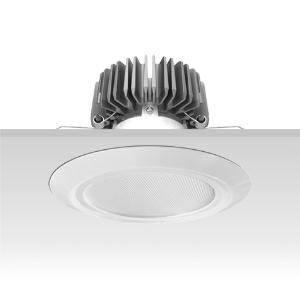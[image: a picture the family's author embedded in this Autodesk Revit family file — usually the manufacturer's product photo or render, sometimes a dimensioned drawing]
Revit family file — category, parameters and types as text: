
# Revit family: 3f_filippi_-_3f_reno_bianco_ampio_3f_filippi_-_30633_a01048_-_3f_reno_200_wh_3000-930_wide___smp_wh_855b
name_source: partatom
category: Lighting Fixtures
units: mm (PartAtom-declared; Revit-internal decimal feet)

## family parameters
Cut with Voids When Loaded = No
Host = Face
Light Source = No
Part Type = Normal
Room Calculation Point = No
Round Connector Dimension = Use Diameter
Shared = No

## types (1)
- 3F Filippi - 3F Reno Bianco Ampio (1 x LED, 2320 lm, 37 W, 3000 K)
    Apparent Load = 37 VA
    Approval mark = CE
    CIE Flux Codes = 74 92 98 100 100
    Color Rendering = 90
    Color Temperature = 3000 K
    Control Gear = Electronic ballast
    Default Elevation = 1800 mm
    Description = ILLUMINOTECHNICAL
Luminous efficiency 100% (DLOR 100%, ULOR 0%).
Initial luminous flux of the luminaire 2320 lm.
Direct symmetric wide distribution.
Installation Interdistance Transv.D = 1.06 x hu - Long.D = 1.04 x hu.
Tabular UGR (CIE 117 - 4H-8H; S=0.25H; 70/50/20): RUG 22.5 - 22.3.
Beam angle: 70° - 69°.
Luminous efficacy 63 lm/W.
Lifetime (L90/B10): 30000 h. (tq+25°C)
Lifetime (L85/B10): 50000 h. (tq+25°C)
Lifetime (L70/B10): 80000 h. (tq+25°C)
Sudden decreased luminous flux after 50000 hours: 0% (C0).
Photobiological safety in compliance with IEC/TR 62778: RG0 risk exempt, (IEC 62471).
In compliance with IEC/EN 62722-2-1 - IEC/EN 62717 standards.

SOURCE
Compact LED module 3000/930.
Energy efficiency class (UE 2019/2020 - UE 2019/2015): E.
CIE 13.3 Colour rendering index: CRI >90 (R9 >50%).
IES TM-30 Fidelity Index: Rf = 92 Rg = 101.
CCT nominal colour temperature 3000 K.
Colour initial tolerance (MacAdam): SDCM 3.
Zhaga Book 3 compliant.

MECHANICAL
Passive heat dissipator in die-casting aluminium, oversized, for optimum thermal management of the LED module.
Parabolic element with graduated/concentric rings in white polycarbonate.
Transparent external lens with glossy and satin differentiated surfaces, with a cooling and anti-insect system in methacrylate (PMMA).
Fastening spring clips in stainless steel.
Dimensions: diameter 226 mm, height 146 mm. Weight 1.645 kg.
IP44 protection degree for exposed part, IP20 for recessed part.
Mechanical strength to impacts IK05 (0.7 joule).
Glow-wire test resistance 650°C.

ELECTRICAL
Wiring on a separate unit.
Halogen Free electronic wiring 230V-50/60Hz, power factor 0.95, THD <25%, constant output current, SELV, class II, 1 driver.
Power of the luminaire 37 W.
ENEC - CE.
SAFE FLICKER: PstLM=<1 and SVM=<0.4 (IEC TR 61547-1 and IEC TR 63158), to ensure a more comfortable and safe light.
Luminaire compliant with EN 60598-2-22 for power supply from a centralised emergency system CPSS (Central Power Supply System), not incorporated in the luminaire - high risk areas excluded. The default power and flux are 100% in AC and 100% in DC.
Ambient temperature from 0°C to +25°C.
Temperature class T6 max 85°C.
Relative humidity UR: <85%.

INSTALLATION
Pull-up recessed fitting.
False ceiling carving: 200 mm.
All accessories dedicated to this product are available on the Catalog and on our website www.3F-Filippi.com.

ACCESSORIES
A01048 - Anti-glare microprismatic SMP diffuser in methacrylate (PMMA), locked and in line with the trim, in white polycarbonate.

APPLICATIONS
Suitable product for food production plants (HACCP), IFS (Food Version 6), BRC (GSFS Food Version 7).
Environments: architectural, commercial, exhibition areas, transit areas, corridors, shops, display windows, service areas.
In false ceilings with narrow voids.

WARNING
Luminaire designed for disposal/recycling at end-of-life.
Replaceable (LED only) light source by a professional. Replaceable control gear by a professional.
    Height = 0 mm  [stored 0 ft]
    Lamp = 1 x LED
    Lamp Light Flux = 2320 lm
    Lamp Power = 37 W
    Lamp count = 1
    Length = 226 mm
    Lifetime = 50000 h
    Luminous efficacy = 63 lm/W
    Manufacturer = 3F Filippi
    ModVariant = No
    Model = 3F Filippi - 30633+A01048 - 3F Reno 200 WH 3000-930 WIDE + SMP WH
    Mounting Place = Ceiling
    Mounting Type = Recessed
    Number of Poles = 1
    OnlyDefault = Yes
    Power Factor = 1
    Product Name = 3F Filippi - 3F Reno Bianco Ampio
    Product group = recessed luminaire
    ProductGroupID = 4
    Protection Class = Protection class II
    Protection Degree = IP 20
    RLX_Detail_Level = 1
    RLX_Emergency_Light_Flux = 0 lm
    RLX_Emergency_Type = 0
    RLX_Emergency_Type_DB = No
    RlxData = <blob elided: 94253 chars, md5=402215c9>
    Socket = socket
    Standby Power = 0 W
    System Light Flux = 2320 lm
    System Power = 37 W
    Type Comments = Product without accessories
    Type Image = 3ffilippi_3f_reno_200_wh_vs_smp.jpg
    URL = http://relux.com
    VarID = ---
    Voltage = 0 V
    Weight = 0.00 kg
    Width = 0 mm  [stored 0 ft]

note: [stored X ft] marks values corroborated as IEEE doubles in the binary element streams (Revit-internal decimal feet)

## geometry (parser evidence)
native form markers: Blend x4, Sweep x9
no freeform markers — native parametric forms only
